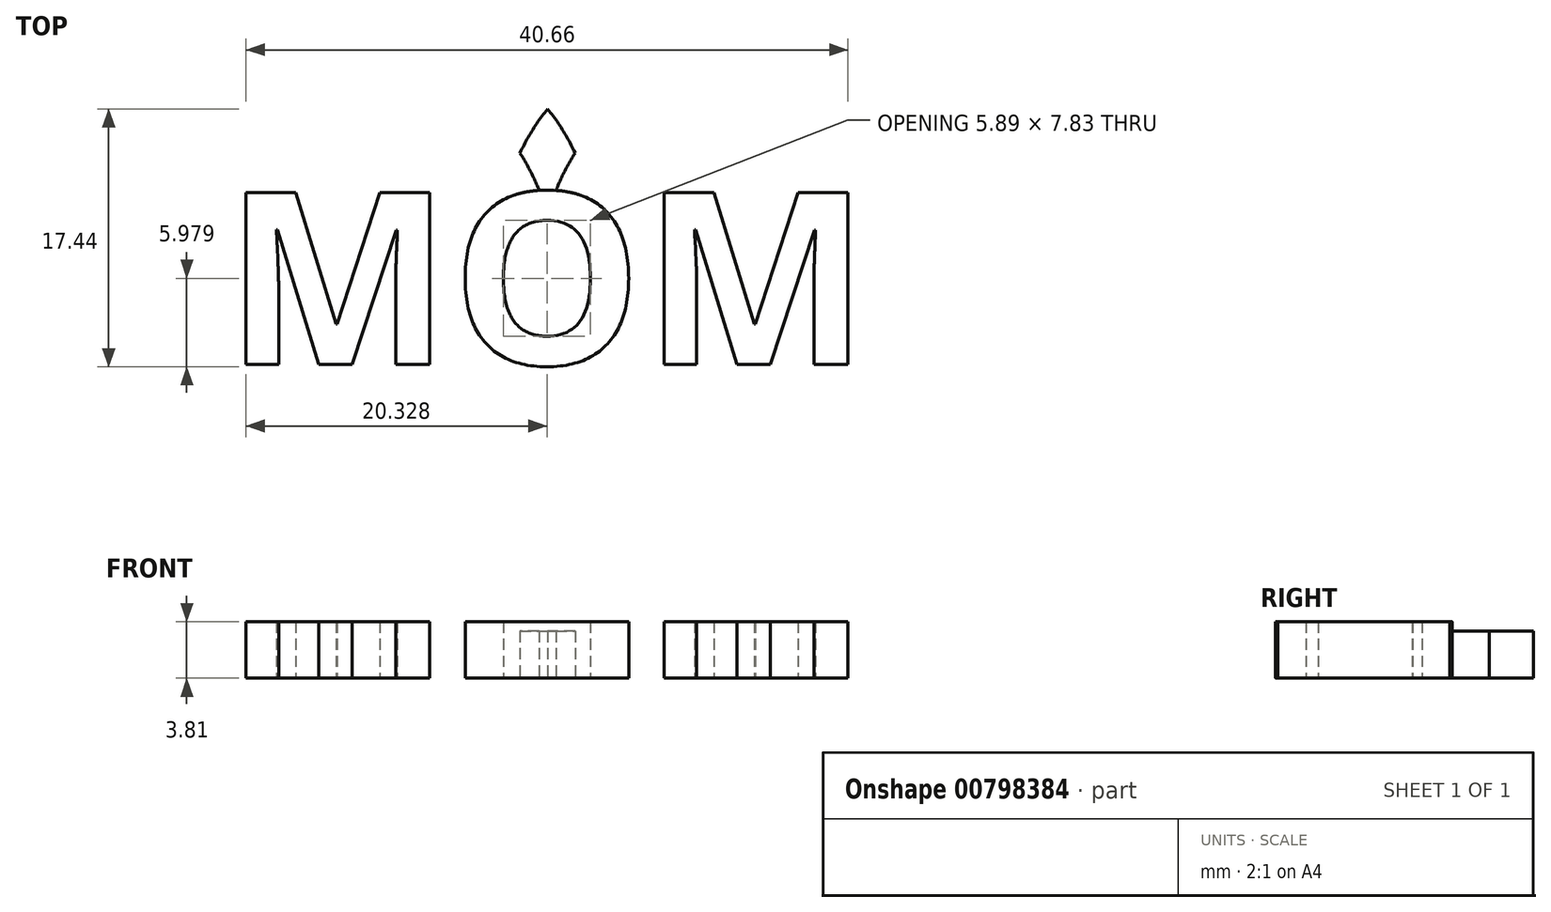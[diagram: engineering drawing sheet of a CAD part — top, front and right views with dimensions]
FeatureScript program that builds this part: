
annotation { "Feature Type Name" : "Feature", "Feature Type Description" : "" }
export const myFeature = defineFeature(function(context is Context, id is Id, definition is map)
    precondition{}
    {
        {
            var Q0;
            Q0=qCreatedBy(makeId("Top.planeOp"),FACE);
            var sketch = newSketch(context, id + "F0", { "sketchPlane" : qUnion([Q0])});
            skFitSpline(sketch, "E0", {"points": [v(0, 9.81) * mm, v(8.48, 19.53) * mm, v(20.23, 10.31) * mm, v(0, -18.87) * mm], "startDerivative": vector(6.85, 38.2) * mm, "endDerivative": vector(-45.05, 0) * mm});
            skLineSegment(sketch, "E1", {"start": v(0, 0) * mm, "end": v(0, 14.87) * mm, "construction": true});
            skFitSpline(sketch, "E2.MirrorCS", {"points": [v(0, 9.81) * mm, v(-8.48, 19.53) * mm, v(-20.23, 10.31) * mm, v(0, -18.87) * mm], "startDerivative": vector(-6.85, 38.2) * mm, "endDerivative": vector(45.05, 0) * mm});
            skPoint(sketch, "E3", {"position": v(0, 7.44) * mm});
            skCircle(sketch, "E4", {"center": v(-9.81, 9.81) * mm, "radius": 9.81 * mm, "construction": true});
            skLineSegment(sketch, "E5", {"start": v(0, 0) * mm, "end": v(-23.85, 0) * mm, "construction": true});
            skCircle(sketch, "E6.MirrorC", {"center": v(9.81, 9.81) * mm, "radius": 9.81 * mm, "construction": true});
            skFitSpline(sketch, "E7.0", {"points": [v(3.13, 10.37) * mm, v(3.02, 10.93) * mm, v(2.74, 12.05) * mm, v(1.86, 14.3) * mm, v(0.56, 16.53) * mm, v(-1.17, 18.63) * mm, v(-2.68, 20.07) * mm, v(-4.15, 21.12) * mm, v(-5.44, 21.81) * mm, v(-6.48, 22.26) * mm, v(-7.4, 22.54) * mm, v(-8.15, 22.72) * mm, v(-9.29, 22.92) * mm, v(-11.02, 23) * mm, v(-13.3, 22.68) * mm, v(-15.5, 21.96) * mm, v(-17.6, 20.85) * mm, v(-19.48, 19.36) * mm, v(-21.11, 17.5) * mm, v(-22.17, 15.63) * mm, v(-22.8, 13.98) * mm, v(-23.15, 12.66) * mm, v(-23.37, 11.29) * mm, v(-23.44, 9.85) * mm, v(-23.39, 8.4) * mm, v(-23.16, 6.47) * mm, v(-22.6, 4.02) * mm, v(-21.6, 1.06) * mm, v(-19.9, -2.9) * mm, v(-17.15, -7.75) * mm, v(-13.9, -12.2) * mm, v(-11.16, -15.34) * mm, v(-9.05, -17.44) * mm, v(-6.92, -19.23) * mm, v(-4.77, -20.67) * mm, v(-2.9, -21.54) * mm, v(-1.3, -21.96) * mm, v(-0.44, -22.04) * mm, v(0, -22.04) * mm]});
            skFitSpline(sketch, "E7.1", {"points": [v(-3.13, 10.37) * mm, v(-3.02, 10.93) * mm, v(-2.74, 12.05) * mm, v(-1.86, 14.3) * mm, v(-0.56, 16.53) * mm, v(1.17, 18.63) * mm, v(2.68, 20.07) * mm, v(4.15, 21.12) * mm, v(5.44, 21.81) * mm, v(6.48, 22.26) * mm, v(7.4, 22.54) * mm, v(8.15, 22.72) * mm, v(9.29, 22.92) * mm, v(11.02, 23) * mm, v(13.3, 22.68) * mm, v(15.5, 21.96) * mm, v(17.6, 20.85) * mm, v(19.48, 19.36) * mm, v(21.11, 17.5) * mm, v(22.17, 15.63) * mm, v(22.8, 13.98) * mm, v(23.15, 12.66) * mm, v(23.37, 11.29) * mm, v(23.44, 9.85) * mm, v(23.39, 8.4) * mm, v(23.16, 6.47) * mm, v(22.6, 4.02) * mm, v(21.6, 1.06) * mm, v(19.9, -2.9) * mm, v(17.15, -7.75) * mm, v(13.9, -12.2) * mm, v(11.16, -15.34) * mm, v(9.05, -17.44) * mm, v(6.92, -19.23) * mm, v(4.77, -20.67) * mm, v(2.9, -21.54) * mm, v(1.3, -21.96) * mm, v(0.44, -22.04) * mm, v(0, -22.04) * mm]});
            skSolve(sketch);
        }
        {
            var Q0;
            Q0=makeQuery(id+"F0.imprint","IMPRINT",FACE,{"disambiguationData":[TD([[makeQuery(id+"F0.imprint","IMPRINT",EDGE,{"derivedFrom":sQuery(id+"F0.wireOp",EDGE,"E0")}),1.0]])]});
            extrude(context, id + "F1", {"entities" : qUnion([Q0]), "depth" : 3.17 * mm, "offsetDistance" : 25.4 * mm});
        }
        {
            var Q0;
            Q0=qCreatedBy(makeId("Top.planeOp"),FACE);
            var sketch = newSketch(context, id + "F2", { "sketchPlane" : qUnion([Q0])});
            skLineSegment(sketch, "E8", {"start": v(0, 0) * mm, "end": v(0, 22.98) * mm, "construction": true});
            skLineSegment(sketch, "E9", {"start": v(0, 0) * mm, "end": v(25.61, 0) * mm, "construction": true});
            skText(sketch, "E10", { "text": "MOM", "fontName": "OpenSans-Bold.ttf"});
            const initialGuessF2  = {"E10": [-0.02183, 0, 1, 0, 0.0117]};
            skSetInitialGuess(sketch, initialGuessF2);
            skSolve(sketch);
        }
        {
            var Q0;
            Q0=makeQuery(id+"F2.imprint","IMPRINT",FACE,{"disambiguationData":[TD([[makeQuery(id+"F2.imprint","IMPRINT",EDGE,{"derivedFrom":sQuery(id+"F2.wireOp",EDGE,"E10.sketch_text.stroke-19")}),-1.0]])]});
            var Q1;
            Q1=makeQuery(id+"F2.imprint","IMPRINT",FACE,{"disambiguationData":[TD([[makeQuery(id+"F2.imprint","IMPRINT",EDGE,{"derivedFrom":sQuery(id+"F2.wireOp",EDGE,"E10.sketch_text.stroke-33")}),-1.0]])]});
            var Q2;
            Q2=makeQuery(id+"F2.imprint","IMPRINT",FACE,{"disambiguationData":[TD([[makeQuery(id+"F2.imprint","IMPRINT",EDGE,{"derivedFrom":sQuery(id+"F2.wireOp",EDGE,"E10.sketch_text.stroke-0")}),-1.0]])]});
            extrude(context, id + "F3", {"entities" : qUnion([Q0, Q1, Q2]), "operationType" : NewBodyOperationType.ADD, "depth" : 3.8 * mm, "offsetDistance" : 25.4 * mm});
        }
    });
